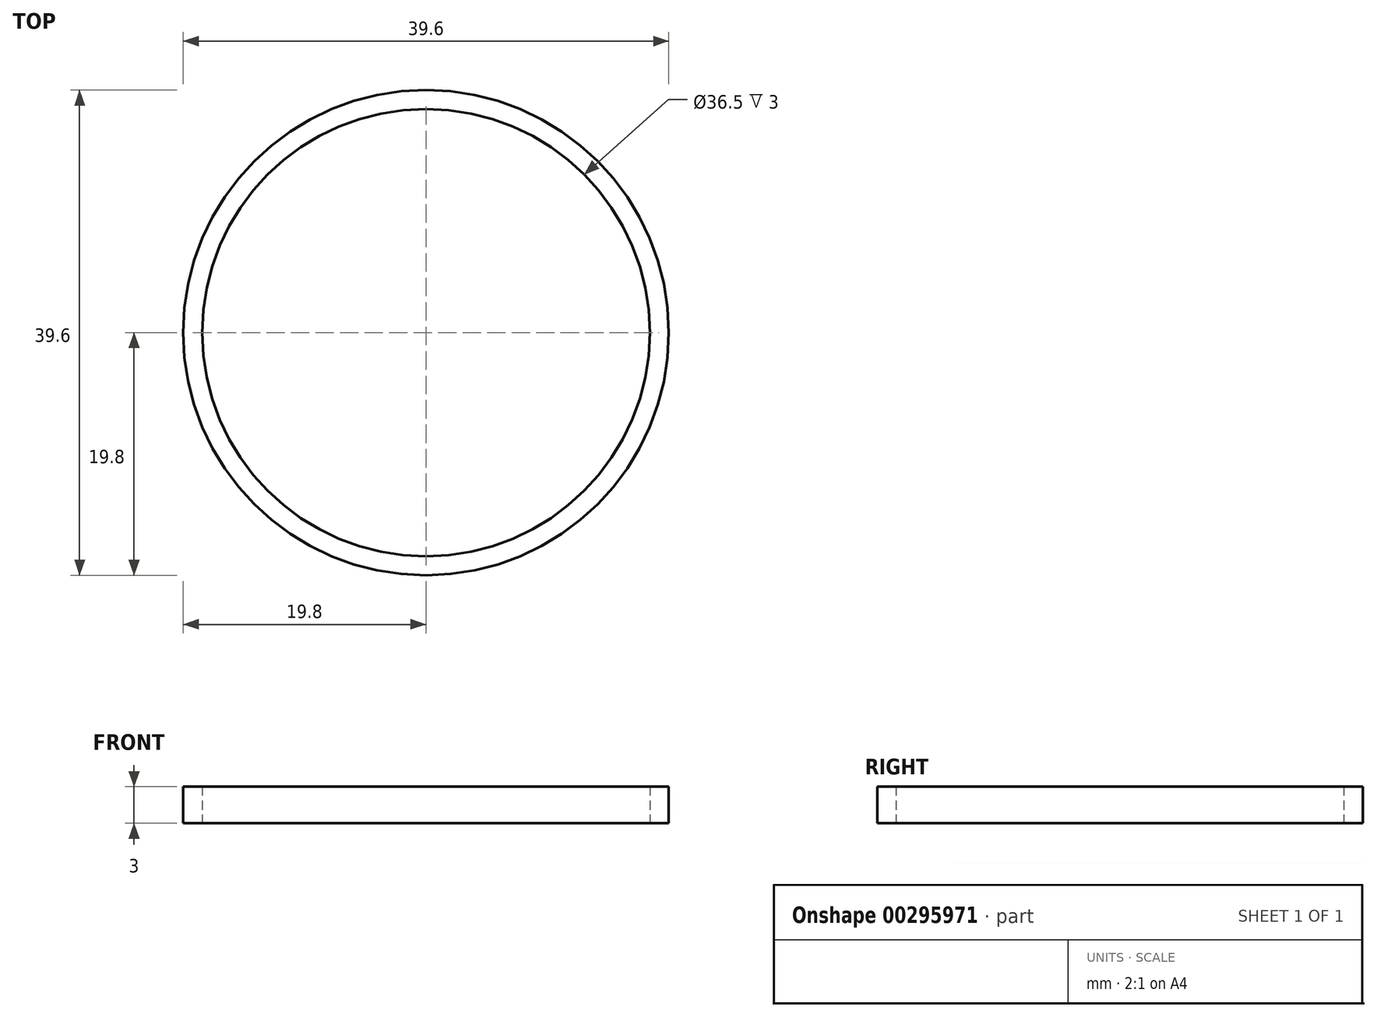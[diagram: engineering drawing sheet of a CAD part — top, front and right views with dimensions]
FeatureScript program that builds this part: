
annotation { "Feature Type Name" : "Feature", "Feature Type Description" : "" }
export const myFeature = defineFeature(function(context is Context, id is Id, definition is map)
    precondition{}
    {
        {
            var Q0;
            Q0=qCreatedBy(makeId("Top.planeOp"),FACE);
            var sketch = newSketch(context, id + "F0", { "sketchPlane" : qUnion([Q0])});
            skCircle(sketch, "E0", {"center": v(0, 0) * mm, "radius": 19.8 * mm});
            skCircle(sketch, "E1", {"center": v(0, 0) * mm, "radius": 18.25 * mm});
            skSolve(sketch);
        }
        {
            var Q0;
            Q0=makeQuery(id+"F0.imprint","IMPRINT",FACE,{"disambiguationData":[TD([[makeQuery(id+"F0.imprint","IMPRINT",EDGE,{"derivedFrom":sQuery(id+"F0.wireOp",EDGE,"E0")}),1.0]])]});
            extrude(context, id + "F1", {"entities" : qUnion([Q0]), "depth" : 3 * mm});
        }
    });
